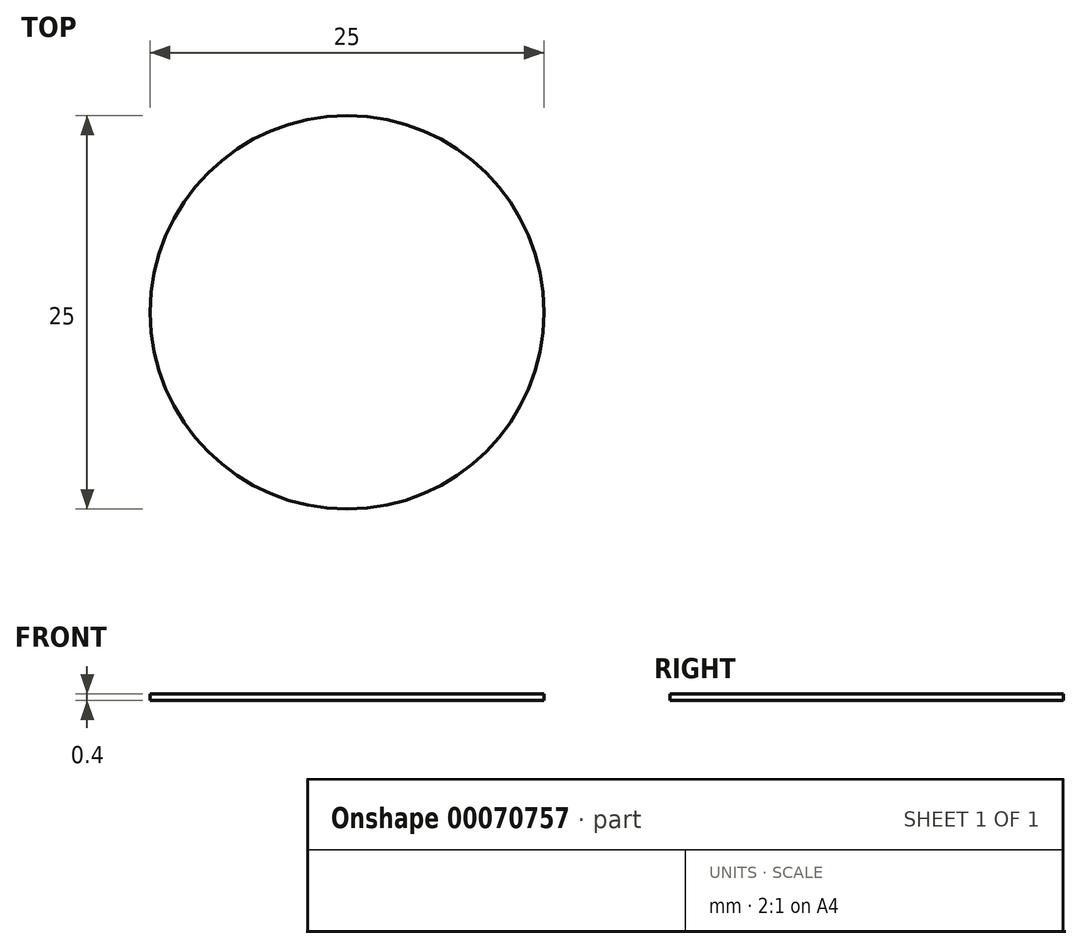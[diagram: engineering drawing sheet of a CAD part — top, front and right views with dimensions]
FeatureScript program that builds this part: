
annotation { "Feature Type Name" : "Feature", "Feature Type Description" : "" }
export const myFeature = defineFeature(function(context is Context, id is Id, definition is map)
    precondition{}
    {
        {
            var Q0;
            Q0=qCreatedBy(makeId("Top.planeOp"),FACE);
            var sketch = newSketch(context, id + "F0", { "sketchPlane" : qUnion([Q0])});
            skCircle(sketch, "E0", {"center": v(0.13, -0.65) * mm, "radius": 12.5 * mm});
            skSolve(sketch);
        }
        {
            var Q0;
            Q0=makeQuery(id+"F0.imprint","IMPRINT",FACE,{"disambiguationData":[TD([[makeQuery(id+"F0.imprint","IMPRINT",EDGE,{"derivedFrom":sQuery(id+"F0.wireOp",EDGE,"E0")}),1.0]])]});
            extrude(context, id + "F1", {"entities" : qUnion([Q0]), "depth" : 0.4 * mm});
        }
    });
